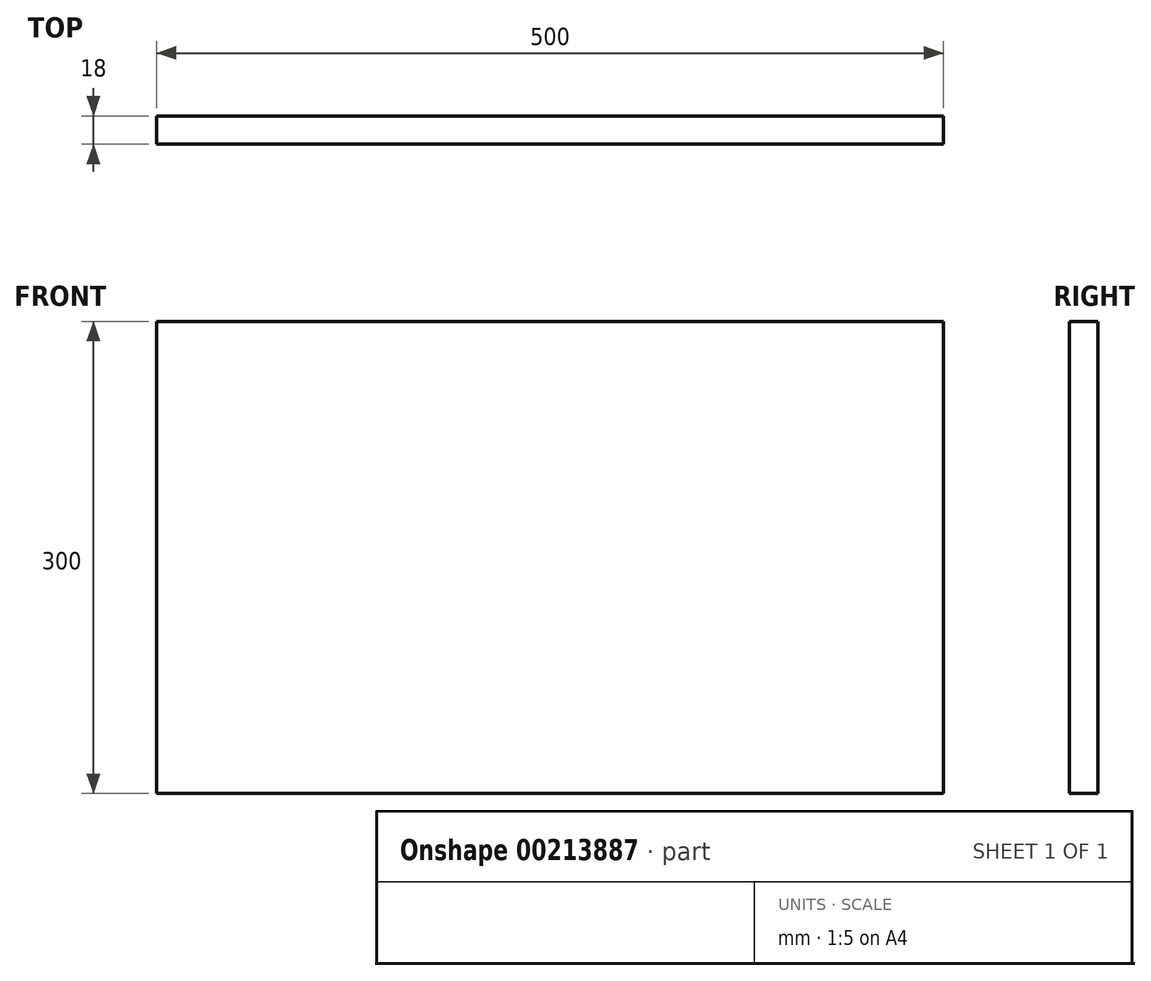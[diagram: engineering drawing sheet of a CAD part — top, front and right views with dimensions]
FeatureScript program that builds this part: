
annotation { "Feature Type Name" : "Feature", "Feature Type Description" : "" }
export const myFeature = defineFeature(function(context is Context, id is Id, definition is map)
    precondition{}
    {
        {
            var Q0;
            Q0=qCreatedBy(makeId("Front.planeOp"),FACE);
            var sketch = newSketch(context, id + "F0", { "sketchPlane" : qUnion([Q0])});
            skLineSegment(sketch, "E0.bottom", {"start": v(-320.4, 233.7) * mm, "end": v(179.6, 233.7) * mm});
            skLineSegment(sketch, "E0.top", {"start": v(-320.4, -66.3) * mm, "end": v(179.6, -66.3) * mm});
            skLineSegment(sketch, "E0.left", {"start": v(-320.4, 233.7) * mm, "end": v(-320.4, -66.3) * mm});
            skLineSegment(sketch, "E0.right", {"start": v(179.6, 233.7) * mm, "end": v(179.6, -66.3) * mm});
            skSolve(sketch);
        }
        {
            var Q0;
            Q0=makeQuery(id+"F0.imprint","IMPRINT",FACE,{"disambiguationData":[TD([[makeQuery(id+"F0.imprint","IMPRINT",EDGE,{"derivedFrom":sQuery(id+"F0.wireOp",EDGE,"E0.bottom")}),-1.0]])]});
            extrude(context, id + "F1", {"entities" : qUnion([Q0]), "depth" : 18 * mm, "offsetDistance" : 25 * mm});
        }
    });
